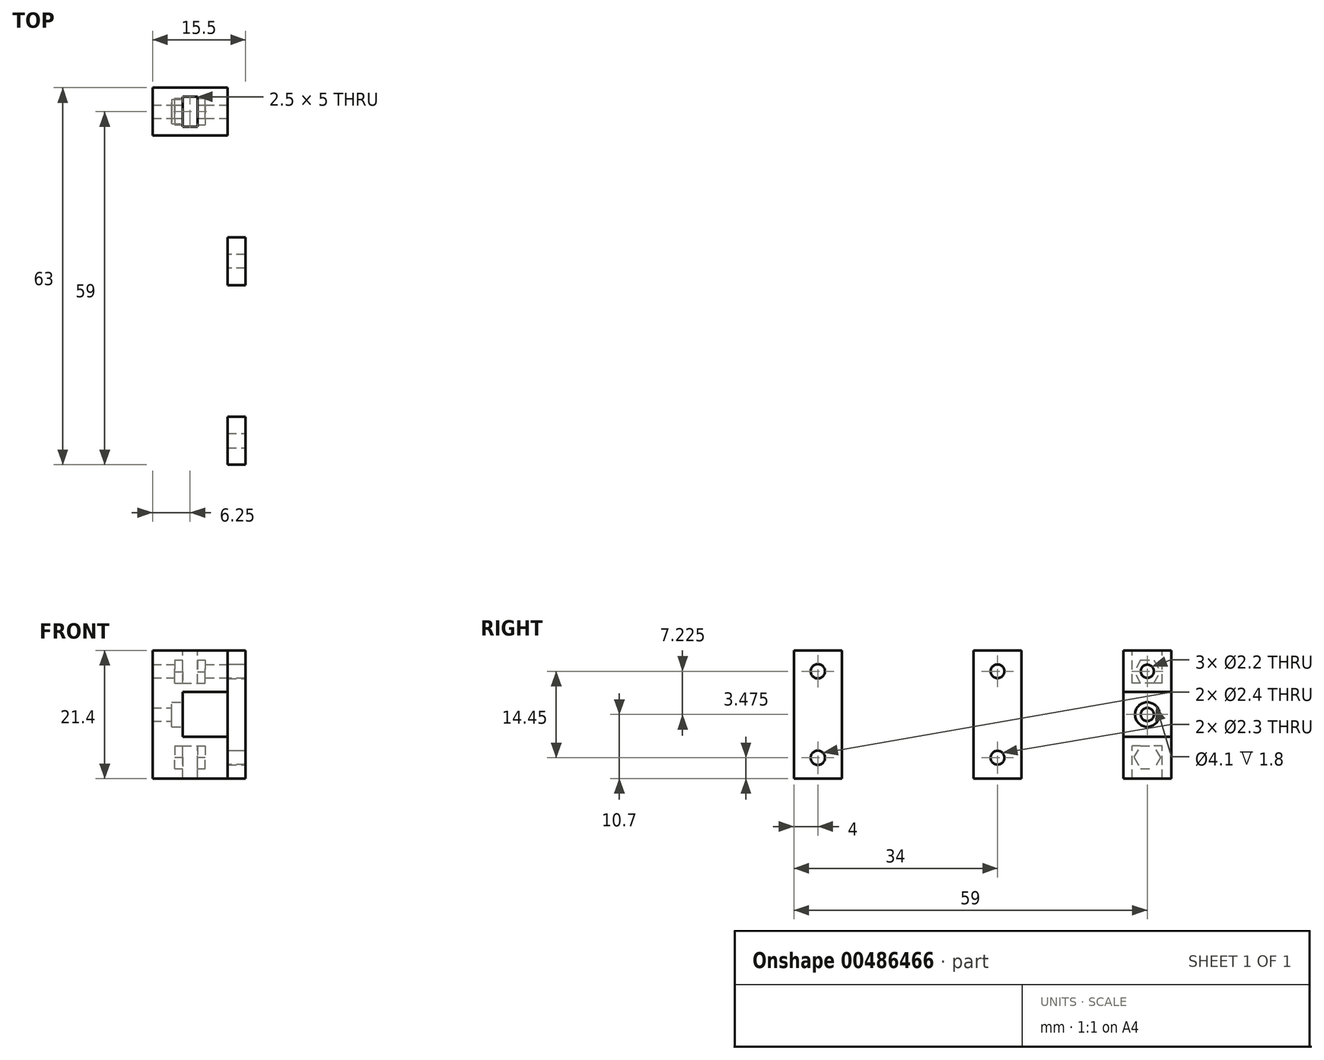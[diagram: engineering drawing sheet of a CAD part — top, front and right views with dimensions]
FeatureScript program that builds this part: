
annotation { "Feature Type Name" : "Feature", "Feature Type Description" : "" }
export const myFeature = defineFeature(function(context is Context, id is Id, definition is map)
    precondition{}
    {
        {
            assignVariable(context, id + "F0", {"name" : "nut_distance", "anyValue" : 5 * mm});
        }
        {
            var Q0;
            Q0=qCreatedBy(makeId("Front.planeOp"),FACE);
            var sketch = newSketch(context, id + "F1", { "sketchPlane" : qUnion([Q0])});
            skLineSegment(sketch, "E0", {"start": v(0, 3.75) * mm, "end": v(-7.5, 3.75) * mm});
            skLineSegment(sketch, "E1", {"start": v(-7.5, -3.75) * mm, "end": v(-7.5, 3.75) * mm});
            skLineSegment(sketch, "E2", {"start": v(-7.5, -3.75) * mm, "end": v(0, -3.75) * mm});
            skLineSegment(sketch, "E3", {"start": v(0, -10.7) * mm, "end": v(0, -3.75) * mm});
            skLineSegment(sketch, "E4", {"start": v(0, -10.7) * mm, "end": v(-12.5, -10.7) * mm});
            skLineSegment(sketch, "E5", {"start": v(-12.5, -10.7) * mm, "end": v(-12.5, 10.7) * mm});
            skLineSegment(sketch, "E6", {"start": v(0, 3.75) * mm, "end": v(0, 10.7) * mm});
            skLineSegment(sketch, "E7", {"start": v(-12.5, 10.7) * mm, "end": v(0, 10.7) * mm});
            skSolve(sketch);
        }
        {
            var Q0;
            Q0=qSketchRegion(id+"F1",true);
            extrude(context, id + "F2", {"entities" : qUnion([Q0]), "depth" : 8 * mm, "offsetDistance" : 25 * mm, "symmetric" : true});
        }
        {
            var Q0;
            Q0=makeQuery(id+"F2.opExtrude","SWEPT_FACE",FACE,{"disambiguationData":[OSD([sQuery(id+"F1.wireOp",EDGE,"E6")])]});
            var sketch = newSketch(context, id + "F3", { "sketchPlane" : qUnion([Q0])});
            skLineSegment(sketch, "E8", {"start": v(-12.42, 0) * mm, "end": v(17.97, 0) * mm, "construction": true});
            skLineSegment(sketch, "E9", {"start": v(0, 22.03) * mm, "end": v(0, -15.29) * mm, "construction": true});
            skPoint(sketch, "E9.startSnap0", {"position": v(0, 10.7) * mm});
            skLineSegment(sketch, "E10", {"start": v(0, 5.25) * mm, "end": v(-1.1, 5.25) * mm});
            skLineSegment(sketch, "E11", {"start": v(-1.1, 5.25) * mm, "end": v(-2.21, 7.16) * mm});
            skLineSegment(sketch, "E12", {"start": v(-2.21, 7.16) * mm, "end": v(0, 7.16) * mm, "construction": true});
            skLineSegment(sketch, "E13", {"start": v(0, 7.16) * mm, "end": v(1.1, 5.25) * mm, "construction": true});
            skLineSegment(sketch, "E14.MirrorCS", {"start": v(-1.1, 9.08) * mm, "end": v(-2.21, 7.16) * mm});
            skLineSegment(sketch, "E15.MirrorCS", {"start": v(0, 9.08) * mm, "end": v(-1.1, 9.08) * mm});
            skLineSegment(sketch, "E16.MirrorCS", {"start": v(0, 9.08) * mm, "end": v(1.1, 9.08) * mm});
            skLineSegment(sketch, "E17.MirrorCS", {"start": v(1.1, 9.08) * mm, "end": v(2.21, 7.17) * mm});
            skLineSegment(sketch, "E18.MirrorCS", {"start": v(1.1, 5.25) * mm, "end": v(2.21, 7.17) * mm});
            skLineSegment(sketch, "E19.MirrorCS", {"start": v(0, 5.25) * mm, "end": v(1.1, 5.25) * mm});
            skLineSegment(sketch, "E20.MirrorCS", {"start": v(-1.1, -9.08) * mm, "end": v(-2.21, -7.16) * mm});
            skLineSegment(sketch, "E21.MirrorCS", {"start": v(0, -9.08) * mm, "end": v(-1.1, -9.08) * mm});
            skLineSegment(sketch, "E22.MirrorCS", {"start": v(0, -9.08) * mm, "end": v(1.1, -9.08) * mm});
            skLineSegment(sketch, "E23.MirrorCS", {"start": v(1.1, -9.08) * mm, "end": v(2.21, -7.17) * mm});
            skLineSegment(sketch, "E24.MirrorCS", {"start": v(1.1, -5.25) * mm, "end": v(2.21, -7.17) * mm});
            skLineSegment(sketch, "E25.MirrorCS", {"start": v(0, -5.25) * mm, "end": v(1.1, -5.25) * mm});
            skLineSegment(sketch, "E26.MirrorCS", {"start": v(0, -5.25) * mm, "end": v(-1.1, -5.25) * mm});
            skLineSegment(sketch, "E27.MirrorCS", {"start": v(-1.1, -5.25) * mm, "end": v(-2.21, -7.16) * mm});
            skSolve(sketch);
        }
        {
            var Q0;
            Q0=makeQuery(id+"F3.imprint","IMPRINT",FACE,{"disambiguationData":[TD([[makeQuery(id+"F3.imprint","IMPRINT",EDGE,{"derivedFrom":sQuery(id+"F3.wireOp",EDGE,"E10")}),-1.0]])]});
            var Q1;
            Q1=makeQuery(id+"F3.imprint","IMPRINT",FACE,{"disambiguationData":[TD([[makeQuery(id+"F3.imprint","IMPRINT",EDGE,{"derivedFrom":sQuery(id+"F3.wireOp",EDGE,"E20.MirrorCS")}),-1.0]])]});
            extrude(context, id + "F4", {"entities" : qUnion([Q0, Q1]), "operationType" : NewBodyOperationType.REMOVE, "oppositeDirection" : true, "depth" : 5.4 * mm, "hasOffset" : true, "offsetDistance" : 4 * mm, "hasSecondDirection" : true, "secondDirectionOppositeDirection" : true, "secondDirectionDepth" : getVariable(context, 'nut_distance') - 1.3 * mm});
        }
        {
            var Q0;
            Q0=makeQuery(id+"F2.opExtrude","SWEPT_FACE",FACE,{"disambiguationData":[OSD([sQuery(id+"F1.wireOp",EDGE,"E7")])]});
            var sketch = newSketch(context, id + "F5", { "sketchPlane" : qUnion([Q0])});
            skLineSegment(sketch, "E28.bottom", {"start": v(-7.5, 2.5) * mm, "end": v(-5, 2.5) * mm});
            skLineSegment(sketch, "E28.top", {"start": v(-7.5, -2.5) * mm, "end": v(-5, -2.5) * mm});
            skLineSegment(sketch, "E28.left", {"start": v(-7.5, 2.5) * mm, "end": v(-7.5, -2.5) * mm});
            skLineSegment(sketch, "E28.right", {"start": v(-5, 2.5) * mm, "end": v(-5, -2.5) * mm});
            skSolve(sketch);
        }
        {
            var Q0;
            Q0=qSketchRegion(id+"F5",true);
            var Q1;
            Q1=makeQuery(id+"F4.boolean.opBoolean","COPY",VERTEX,{"derivedFrom":makeQuery(id+"F4.opExtrude","CAP_VERTEX",VERTEX,{"disambiguationData":[OSD([sQuery(id+"F3.wireOp",EDGE,"E10"),sQuery(id+"F3.wireOp",EDGE,"E11")])],"isStart":false})});
            extrude(context, id + "F6", {"entities" : qUnion([Q0]), "operationType" : NewBodyOperationType.REMOVE, "endBound" : BoundingType.UP_TO_VERTEX, "oppositeDirection" : true, "depth" : 25 * mm, "endBoundEntityVertex" : qUnion([Q1]), "offsetDistance" : 25 * mm});
        }
        {
            var Q0;
            Q0=makeQuery(id+"F2.opExtrude","SWEPT_FACE",FACE,{"disambiguationData":[OSD([sQuery(id+"F1.wireOp",EDGE,"E6")])]});
            var sketch = newSketch(context, id + "F7", { "sketchPlane" : qUnion([Q0])});
            skCircle(sketch, "E29", {"center": v(0, 7.22) * mm, "radius": 1.1 * mm});
            skCircle(sketch, "E30.MirrorC", {"center": v(0, -7.22) * mm, "radius": 1.1 * mm});
            skSolve(sketch);
        }
        {
            var Q0;
            Q0=makeQuery(id+"F7.imprint","IMPRINT",FACE,{"disambiguationData":[TD([[makeQuery(id+"F7.imprint","IMPRINT",EDGE,{"derivedFrom":sQuery(id+"F7.wireOp",EDGE,"E29")}),1.0]])]});
            var Q1;
            Q1=makeQuery(id+"F7.imprint","IMPRINT",FACE,{"disambiguationData":[TD([[makeQuery(id+"F7.imprint","IMPRINT",EDGE,{"derivedFrom":sQuery(id+"F7.wireOp",EDGE,"E30.MirrorC")}),-1.0]])]});
            var Q2;
            Q2=makeQuery(id+"F4.boolean.opBoolean","COPY",VERTEX,{"derivedFrom":makeQuery(id+"F4.opExtrude","CAP_VERTEX",VERTEX,{"disambiguationData":[OSD([sQuery(id+"F3.wireOp",EDGE,"E17.MirrorCS"),sQuery(id+"F3.wireOp",EDGE,"E18.MirrorCS")])],"isStart":false})});
            extrude(context, id + "F8", {"entities" : qUnion([Q0, Q1]), "operationType" : NewBodyOperationType.REMOVE, "endBound" : BoundingType.THROUGH_ALL, "oppositeDirection" : true, "depth" : 25 * mm, "endBoundEntityVertex" : qUnion([Q2]), "offsetDistance" : 25 * mm});
        }
        {
            var Q0;
            Q0=qSketchRegion(id+"F5",true);
            var Q1;
            Q1=makeQuery(id+"F2.opExtrude","SWEPT_FACE",FACE,{"disambiguationData":[OSD([sQuery(id+"F1.wireOp",EDGE,"E4")])]});
            var Q2;
            Q2=makeQuery(id+"F4.boolean.opBoolean","COPY",VERTEX,{"derivedFrom":makeQuery(id+"F4.opExtrude","CAP_VERTEX",VERTEX,{"disambiguationData":[OSD([sQuery(id+"F3.wireOp",EDGE,"E26.MirrorCS"),sQuery(id+"F3.wireOp",EDGE,"E27.MirrorCS")])],"isStart":false})});
            extrude(context, id + "F9", {"entities" : qUnion([Q0]), "operationType" : NewBodyOperationType.REMOVE, "endBound" : BoundingType.UP_TO_SURFACE, "oppositeDirection" : true, "depth" : 25 * mm, "endBoundEntityFace" : qUnion([Q1]), "offsetDistance" : 25 * mm, "hasSecondDirection" : true, "secondDirectionBound" : BoundingType.UP_TO_VERTEX, "secondDirectionOppositeDirection" : true, "secondDirectionDepth" : 25 * mm, "secondDirectionBoundEntityVertex" : qUnion([Q2])});
        }
        {
            var Q0;
            Q0 = qSketchRegion(id + "F3", true);
            extrude(context, id + "F10", {"entities" : qUnion([Q0]), "operationType" : NewBodyOperationType.REMOVE, "oppositeDirection" : true, "depth" : (7.5 + 1.3) * mm, "offsetDistance" : 25 * mm, "hasSecondDirection" : true, "secondDirectionOppositeDirection" : true, "secondDirectionDepth" : (5.4 + 1.7) * mm});
        }
        {
            var Q0;
            Q0=makeQuery(id+"F2.opExtrude","SWEPT_FACE",FACE,{"disambiguationData":[OSD([sQuery(id+"F1.wireOp",EDGE,"E1")])]});
            var sketch = newSketch(context, id + "F11", { "sketchPlane" : qUnion([Q0])});
            skCircle(sketch, "E31", {"center": v(0, 0) * mm, "radius": 1.1 * mm});
            skSolve(sketch);
        }
        {
            var Q0;
            Q0=makeQuery(id+"F11.imprint","IMPRINT",FACE,{"disambiguationData":[TD([[makeQuery(id+"F11.imprint","IMPRINT",EDGE,{"derivedFrom":sQuery(id+"F11.wireOp",EDGE,"E31")}),-1.0]])]});
            var sketch = newSketch(context, id + "F12", { "sketchPlane" : qUnion([Q0])});
            skCircle(sketch, "E32", {"center": v(0, 0) * mm, "radius": 2.05 * mm});
            skSolve(sketch);
        }
        {
            var Q0;
            Q0 = qSketchRegion(id + "F11", true);
            extrude(context, id + "F13", {"entities" : qUnion([Q0]), "operationType" : NewBodyOperationType.REMOVE, "endBound" : BoundingType.UP_TO_NEXT, "oppositeDirection" : true, "depth" : 25 * mm, "offsetDistance" : 25 * mm});
        }
        {
            var Q0;
            Q0 = qSketchRegion(id + "F12", true);
            extrude(context, id + "F14", {"entities" : qUnion([Q0]), "operationType" : NewBodyOperationType.REMOVE, "oppositeDirection" : true, "depth" : 1.8 * mm, "offsetDistance" : 25 * mm});
        }
        {
            var Q0;
            Q0=qCreatedBy(makeId("Front.planeOp"),FACE);
            cPlane(context, id + "F15", {"entities" : qUnion([Q0]), "cplaneType" : CPlaneType.OFFSET, "offset" : 25 * mm, "width" : 150 * mm, "height" : 150 * mm});
        }
        {
            var Q0;
            Q0=qCreatedBy(makeId("Right.planeOp"),FACE);
            var sketch = newSketch(context, id + "F16", { "sketchPlane" : qUnion([Q0])});
            skLineSegment(sketch, "E33.bottom", {"start": v(-21, 10.7) * mm, "end": v(-29, 10.7) * mm});
            skLineSegment(sketch, "E33.top", {"start": v(-21, -10.7) * mm, "end": v(-29, -10.7) * mm});
            skLineSegment(sketch, "E33.left", {"start": v(-21, 10.7) * mm, "end": v(-21, -10.7) * mm});
            skLineSegment(sketch, "E33.right", {"start": v(-29, 10.7) * mm, "end": v(-29, -10.7) * mm});
            skCircle(sketch, "E34", {"center": v(-25, 7.22) * mm, "radius": 1.15 * mm});
            skCircle(sketch, "E35.MirrorC", {"center": v(-25, -7.22) * mm, "radius": 1.15 * mm});
            skSolve(sketch);
        }
        {
            var Q0;
            Q0=makeQuery(id+"F16.imprint","IMPRINT",FACE,{"disambiguationData":[TD([[makeQuery(id+"F16.imprint","IMPRINT",EDGE,{"derivedFrom":sQuery(id+"F16.wireOp",EDGE,"E33.bottom")}),1.0]])]});
            extrude(context, id + "F17", {"entities" : qUnion([Q0]), "depth" : 3 * mm, "offsetDistance" : 25 * mm});
        }
        {
            var Q0;
            Q0=qCreatedBy(id+"F15.planeOp",FACE);
            var sketch = newSketch(context, id + "F18", { "sketchPlane" : qUnion([Q0])});
            skArc(sketch, "E36", {"start": v(0, 3.75) * mm, "mid": v(-0.1, 0) * mm, "end": v(0, -3.75) * mm});
            skLineSegment(sketch, "E37", {"start": v(0, 3.75) * mm, "end": v(0, -3.75) * mm});
            skSolve(sketch);
        }
        {
            var Q0;
            Q0=makeQuery(id+"F17.opExtrude","SWEPT_BODY",BODY,{"disambiguationData":[OSD([sQuery(id+"F16.wireOp",EDGE,"E33.bottom"),sQuery(id+"F16.wireOp",EDGE,"E33.top"),sQuery(id+"F16.wireOp",EDGE,"E33.left"),sQuery(id+"F16.wireOp",EDGE,"E33.right"),sQuery(id+"F16.wireOp",EDGE,"E34"),sQuery(id+"F16.wireOp",EDGE,"E35.MirrorC")])]});
            transform(context, id + "F19", {"entities" : qUnion([Q0]), "transformType" : TransformType.TRANSLATION_3D, "dx" : 0 * mm, "dy" : -30 * mm, "dz" : 0 * mm, "makeCopy" : true});
        }
        {
            var Q0;
            Q0=makeQuery(id+"F19.opPattern","COPY",FACE,{"derivedFrom":makeQuery(id+"F17.opExtrude","CAP_FACE",FACE,{"disambiguationData":[OSD([sQuery(id+"F16.wireOp",EDGE,"E33.bottom"),sQuery(id+"F16.wireOp",EDGE,"E33.top"),sQuery(id+"F16.wireOp",EDGE,"E33.left"),sQuery(id+"F16.wireOp",EDGE,"E33.right"),sQuery(id+"F16.wireOp",EDGE,"E34"),sQuery(id+"F16.wireOp",EDGE,"E35.MirrorC")])],"isStart":false}),"instanceName":"1"});
            var sketch = newSketch(context, id + "F20", { "sketchPlane" : qUnion([Q0])});
            skCircle(sketch, "E38", {"center": v(-55, 7.22) * mm, "radius": 1.2 * mm});
            skCircle(sketch, "E39.MirrorC", {"center": v(-55, -7.22) * mm, "radius": 1.2 * mm});
            skSolve(sketch);
        }
        {
            var Q0;
            Q0 = qSketchRegion(id + "F20", true);
            extrude(context, id + "F21", {"entities" : qUnion([Q0]), "operationType" : NewBodyOperationType.REMOVE, "endBound" : BoundingType.THROUGH_ALL, "oppositeDirection" : true, "depth" : 25 * mm, "offsetDistance" : 25 * mm});
        }
    });
